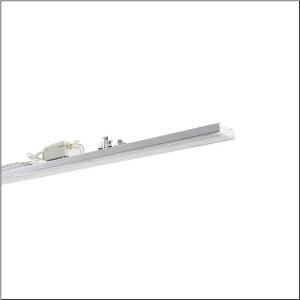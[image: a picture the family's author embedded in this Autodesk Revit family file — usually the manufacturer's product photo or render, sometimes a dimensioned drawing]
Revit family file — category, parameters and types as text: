
# Revit family: licross_r__21_recessed_ho_52te12dv4lxm_5120
name_source: partatom
category: Lighting Fixtures
units: mm (PartAtom-declared; Revit-internal decimal feet)

## family parameters
Cut with Voids When Loaded = No
Host = Face
Light Source = No
Part Type = Normal
Room Calculation Point = No
Round Connector Dimension = Use Diameter
Shared = No

## types (1)
- --- (1 x LED, 20000 lm, 109.8 W, 4000K)
    Apparent Load = 110 VA
    CIE Flux Codes = 69 91 98 100 100
    Color Rendering = 80
    Color Temperature = 4000K
    Default Elevation = 1800 mm
    Description = Licross® 21 Recessed HO, luminaire insert, of sheet steel, galvanised, coil coated, white, length: 2.250mm, width: 66mm, height: 67mm, LED rated luminous flux: 20.000lm, light colour: 840, SDCM (Standard Deviation of Colour Matching)MacAdam ≤ 3 SDCM (initial), control gear: DALI 2, with plug, 5-pole, with phase selection, mains connection: 220..240V, AC, 50/60Hz, rated input power: 110W, internal wiring halogen-free, primary optical cover: cover, of PMMA, light emission: direct distribution, primary light characteristic: symmetric, protection rating (complete): IP54, insulation class (complete): insulation class I (protective earthing), certification: CE, ENEC, VDE, UKCA, protection symbol: D if used in an environment with non-conductive dust loads with corresponding accessories, impact resistance: IK06, permissible ambient temperature for indoor applications: -40..+35°C, corresponds to IFS (International Featured Standards) requirements for safety and quality in the food industry, reducing of maximum allowable ambient temperature of 5°C with ceiling mounting, LABS conformity tested according to VDMA 24364:2018-05, packaging unit: 1 piece
    Height = 58 mm
    Lamp = 1 x LED
    Lamp Light Flux = 20000 lm
    Lamp Power = 109.8 W
    Lamp count = 1
    Length = 2250 mm
    Luminous efficacy = 182 lm/W
    Manufacturer = Siteco
    ModVariant = No
    Model = 52TE12DV4LXM
    Mounting Place = Ceiling
    Mounting Type = Pendant
    Number of Poles = 1
    OnlyDefault = Yes
    Power Factor = 1
    Product Name = Licross® 21 Recessed HO
    Product group = luminaire insert | ceiling pendant
    ProductGroupID = 901
    Protection Class = Protection class I
    Protection Degree = IP 54
    RLX_Detail_Level = 1
    RLX_Emergency_Light_Flux = 0 lm
    RLX_Emergency_Type = 0
    RLX_Emergency_Type_DB = No
    RlxData = <blob elided: 29653 chars, md5=d9af5b9a>
    Socket = socket
    Standby Power = 0 W
    System Light Flux = 20000 lm
    System Power = 110 W
    Type Comments = factory setting: luminous flux: 100 % | dim-lin: 254 | 425 mA
    Type Image = l_1296930.jpg
    URL = http://relux.com
    VarID = @adj_120549
    Voltage = 0 V
    Weight = 0.00 kg
    Width = 66 mm

## geometry (parser evidence)
native form markers: Blend x4, Sweep x9
no freeform markers — native parametric forms only
